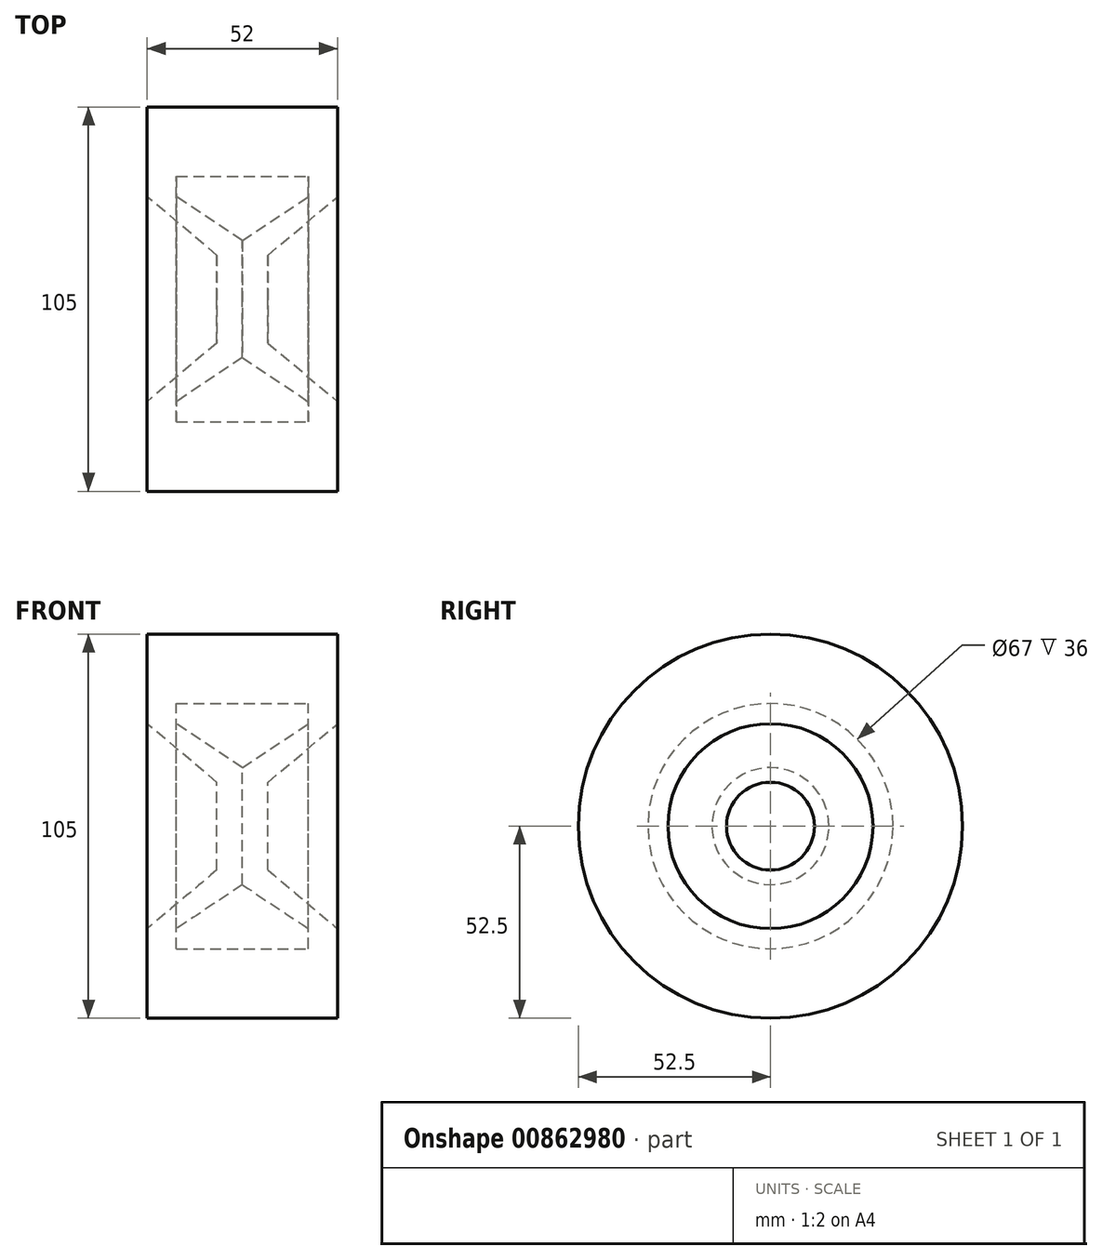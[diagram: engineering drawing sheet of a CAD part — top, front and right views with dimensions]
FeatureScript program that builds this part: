
annotation { "Feature Type Name" : "Feature", "Feature Type Description" : "" }
export const myFeature = defineFeature(function(context is Context, id is Id, definition is map)
    precondition{}
    {
        {
            var Q0;
            Q0=qCreatedBy(makeId("Front.planeOp"),FACE);
            var sketch = newSketch(context, id + "F0", { "sketchPlane" : qUnion([Q0])});
            skLineSegment(sketch, "E0", {"start": v(0, 52.5) * mm, "end": v(26, 52.5) * mm});
            skLineSegment(sketch, "E1", {"start": v(26, 52.5) * mm, "end": v(26, 33.5) * mm});
            skLineSegment(sketch, "E2", {"start": v(26, 33.5) * mm, "end": v(26, 28) * mm});
            skLineSegment(sketch, "E3", {"start": v(26, 28) * mm, "end": v(7, 12) * mm});
            skLineSegment(sketch, "E4", {"start": v(7, 12) * mm, "end": v(7, 0) * mm});
            skLineSegment(sketch, "E5", {"start": v(7, 0) * mm, "end": v(0, 0) * mm});
            skLineSegment(sketch, "E6", {"start": v(0, 0) * mm, "end": v(0, 16) * mm});
            skLineSegment(sketch, "E7", {"start": v(0, 16) * mm, "end": v(18, 28) * mm});
            skLineSegment(sketch, "E8", {"start": v(18, 28) * mm, "end": v(18, 33.5) * mm});
            skLineSegment(sketch, "E9", {"start": v(18, 33.5) * mm, "end": v(0, 33.5) * mm});
            skLineSegment(sketch, "E10", {"start": v(0, 33.5) * mm, "end": v(0, 52.5) * mm});
            skSolve(sketch);
        }
        {
            var Q0;
            Q0 = qSketchRegion(id + "F0", true);
            var Q1;
            Q1=sQuery(id+"F0.wireOp",EDGE,"E5");
            revolve(context, id + "F1", {"surfaceOperationType" : NewSurfaceOperationType.NEW, "entities" : qUnion([Q0]), "axis" : qUnion([Q1]), "revolveType" : RevolveType.FULL});
        }
        {
            var Q0;
            Q0=makeQuery(id+"F1.opRevolve","SWEPT_BODY",BODY,{"disambiguationData":[OSD([sQuery(id+"F0.wireOp",EDGE,"E0"),sQuery(id+"F0.wireOp",EDGE,"E1"),sQuery(id+"F0.wireOp",EDGE,"E2"),sQuery(id+"F0.wireOp",EDGE,"E3"),sQuery(id+"F0.wireOp",EDGE,"E4"),sQuery(id+"F0.wireOp",EDGE,"E5"),sQuery(id+"F0.wireOp",EDGE,"E6"),sQuery(id+"F0.wireOp",EDGE,"E7"),sQuery(id+"F0.wireOp",EDGE,"E8"),sQuery(id+"F0.wireOp",EDGE,"E9"),sQuery(id+"F0.wireOp",EDGE,"E10")])]});
            var Q1;
            Q1=qCreatedBy(makeId("Right.planeOp"),FACE);
            mirror(context, id + "F2", {"operationType" : NewBodyOperationType.ADD, "entities" : qUnion([Q0]), "mirrorPlane" : qUnion([Q1])});
        }
        {
            var Q0;
            Q0=qCreatedBy(makeId("Front.planeOp"),FACE);
            cPlane(context, id + "F3", {"entities" : qUnion([Q0]), "cplaneType" : CPlaneType.OFFSET, "offset" : 52.5 * mm, "width" : 150 * mm, "height" : 150 * mm});
        }
    });
